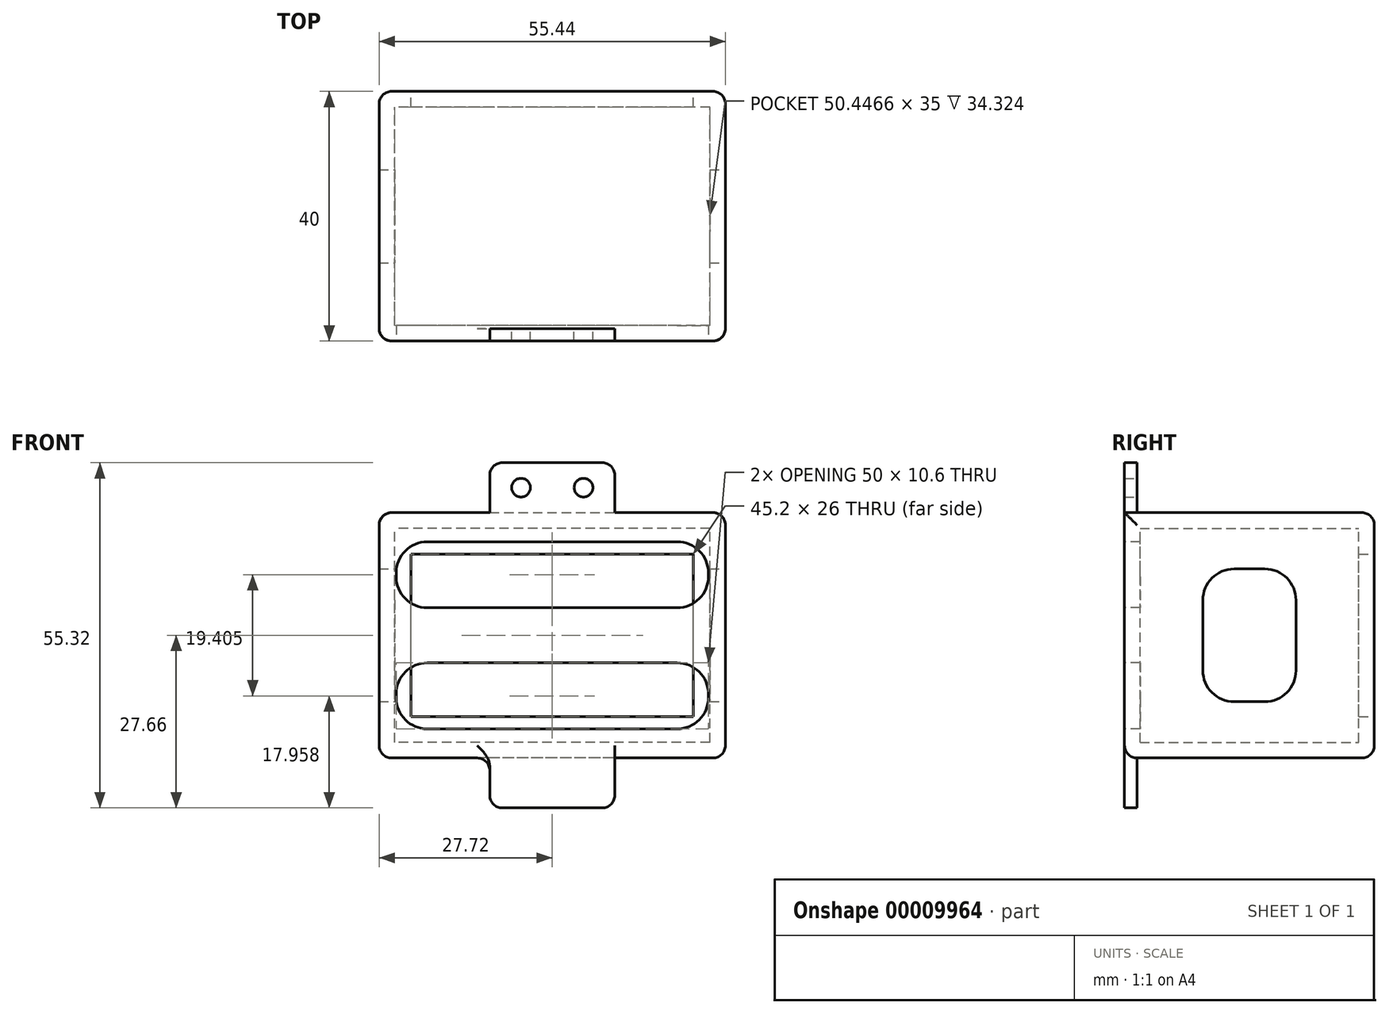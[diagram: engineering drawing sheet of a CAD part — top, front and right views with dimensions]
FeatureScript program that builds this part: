
annotation { "Feature Type Name" : "Feature", "Feature Type Description" : "" }
export const myFeature = defineFeature(function(context is Context, id is Id, definition is map)
    precondition{}
    {
        {
            var Q0;
            Q0=qCreatedBy(makeId("Front.planeOp"),FACE);
            var sketch = newSketch(context, id + "F0", { "sketchPlane" : qUnion([Q0])});
            skLineSegment(sketch, "E0.bottom", {"start": v(0, 0) * mm, "end": v(50, 0) * mm});
            skLineSegment(sketch, "E0.top", {"start": v(0, 30) * mm, "end": v(50, 30) * mm});
            skLineSegment(sketch, "E0.left", {"start": v(0, 0) * mm, "end": v(0, 30) * mm});
            skLineSegment(sketch, "E0.right", {"start": v(50, 0) * mm, "end": v(50, 30) * mm});
            skLineSegment(sketch, "E1", {"start": v(25, 30) * mm, "end": v(25, 0) * mm, "construction": true});
            skLineSegment(sketch, "E2", {"start": v(0, 15) * mm, "end": v(50, 15) * mm, "construction": true});
            skPoint(sketch, "E3", {"position": v(25, 15) * mm});
            skLineSegment(sketch, "E4.rect.bottom", {"start": v(47.6, 2) * mm, "end": v(2.4, 2) * mm});
            skLineSegment(sketch, "E4.rect.top", {"start": v(47.6, 28) * mm, "end": v(2.4, 28) * mm});
            skLineSegment(sketch, "E4.rect.left", {"start": v(47.6, 2) * mm, "end": v(47.6, 28) * mm});
            skLineSegment(sketch, "E4.rect.right", {"start": v(2.4, 2) * mm, "end": v(2.4, 28) * mm});
            skLineSegment(sketch, "E5.rect.bottom", {"start": v(52.72, -4.66) * mm, "end": v(-2.72, -4.66) * mm});
            skLineSegment(sketch, "E5.rect.top", {"start": v(52.72, 34.66) * mm, "end": v(-2.72, 34.66) * mm});
            skLineSegment(sketch, "E5.rect.left", {"start": v(52.72, -4.66) * mm, "end": v(52.72, 34.66) * mm});
            skLineSegment(sketch, "E5.rect.right", {"start": v(-2.72, -4.66) * mm, "end": v(-2.72, 34.66) * mm});
            skSolve(sketch);
        }
        {
            var Q0;
            Q0 = qSketchRegion(id + "F0", true);
            var Q1;
            Q1=makeQuery(id+"F0.imprint","IMPRINT",FACE,{"disambiguationData":[TD([[makeQuery(id+"F0.imprint","IMPRINT",EDGE,{"derivedFrom":sQuery(id+"F0.wireOp",EDGE,"E0.bottom")}),1.0]])]});
            var Q2;
            Q2=makeQuery(id+"F0.imprint","IMPRINT",FACE,{"disambiguationData":[TD([[makeQuery(id+"F0.imprint","IMPRINT",EDGE,{"derivedFrom":sQuery(id+"F0.wireOp",EDGE,"E4.rect.bottom")}),-1.0]])]});
            extrude(context, id + "F1", {"entities" : qUnion([Q0, Q1, Q2]), "depth" : 40 * mm});
        }
        {
            var Q0;
            Q0=makeQuery(id+"F1.opExtrude","CAP_FACE",FACE,{"disambiguationData":[OSD([sQuery(id+"F0.wireOp",EDGE,"E5.rect.bottom"),sQuery(id+"F0.wireOp",EDGE,"E5.rect.top"),sQuery(id+"F0.wireOp",EDGE,"E5.rect.left"),sQuery(id+"F0.wireOp",EDGE,"E5.rect.right")])],"isStart":false});
            var Q1;
            Q1=makeQuery(id+"F1.opExtrude","SWEPT_BODY",BODY,{"disambiguationData":[OSD([sQuery(id+"F0.wireOp",EDGE,"E5.rect.bottom"),sQuery(id+"F0.wireOp",EDGE,"E5.rect.top"),sQuery(id+"F0.wireOp",EDGE,"E5.rect.left"),sQuery(id+"F0.wireOp",EDGE,"E5.rect.right")])]});
            shell(context, id + "F2", {"isHollow" : true, "entities" : qUnion([Q0]), "parts" : qUnion([Q1]), "thickness" : 2.5 * mm});
        }
        {
            var Q0;
            Q0=makeQuery(id+"F0.imprint","IMPRINT",FACE,{"disambiguationData":[TD([[makeQuery(id+"F0.imprint","IMPRINT",EDGE,{"derivedFrom":sQuery(id+"F0.wireOp",EDGE,"E4.rect.bottom")}),-1.0]])]});
            extrude(context, id + "F3", {"entities" : qUnion([Q0]), "operationType" : NewBodyOperationType.REMOVE, "endBound" : BoundingType.UP_TO_NEXT, "depth" : 25 * mm});
        }
        {
            var Q0;
            Q0=makeQuery(id+"F1.opExtrude","CAP_FACE",FACE,{"disambiguationData":[OSD([sQuery(id+"F0.wireOp",EDGE,"E5.rect.bottom"),sQuery(id+"F0.wireOp",EDGE,"E5.rect.top"),sQuery(id+"F0.wireOp",EDGE,"E5.rect.left"),sQuery(id+"F0.wireOp",EDGE,"E5.rect.right")])],"isStart":false});
            var sketch = newSketch(context, id + "F4", { "sketchPlane" : qUnion([Q0])});
            skLineSegment(sketch, "E6.0", {"start": v(5, 30) * mm, "end": v(45, 30) * mm});
            skLineSegment(sketch, "E7.top", {"start": v(5, 19.4) * mm, "end": v(45, 19.4) * mm});
            skLineSegment(sketch, "E7.left", {"start": v(0, 25) * mm, "end": v(0, 24.4) * mm});
            skLineSegment(sketch, "E7.right", {"start": v(50, 25) * mm, "end": v(50, 24.4) * mm});
            skPoint(sketch, "E8.visualSharp", {"position": v(0, 30) * mm});
            skArc(sketch, "E8.filletArc", {"start": v(5, 30) * mm, "mid": v(1.46, 28.54) * mm, "end": v(0, 25) * mm});
            skPoint(sketch, "E9.visualSharp", {"position": v(50, 30) * mm});
            skArc(sketch, "E9.filletArc", {"start": v(50, 25) * mm, "mid": v(48.54, 28.54) * mm, "end": v(45, 30) * mm});
            skPoint(sketch, "E10.visualSharp", {"position": v(0, 19.4) * mm});
            skArc(sketch, "E10.filletArc", {"start": v(0, 24.4) * mm, "mid": v(1.46, 20.87) * mm, "end": v(5, 19.4) * mm});
            skPoint(sketch, "E11.visualSharp", {"position": v(50, 19.4) * mm});
            skArc(sketch, "E11.filletArc", {"start": v(45, 19.4) * mm, "mid": v(48.54, 20.87) * mm, "end": v(50, 24.4) * mm});
            skPoint(sketch, "E12.orphan", {"position": v(25, 0) * mm});
            skPoint(sketch, "E13.0.start.orphan", {"position": v(25, 30) * mm});
            skLineSegment(sketch, "E14.0", {"start": v(0, 15) * mm, "end": v(50, 15) * mm});
            skLineSegment(sketch, "E15.0.MirrorCS", {"start": v(5, 10.6) * mm, "end": v(45, 10.6) * mm});
            skArc(sketch, "E16.0.MirrorCS", {"start": v(45, 10.6) * mm, "mid": v(48.54, 9.13) * mm, "end": v(50, 5.6) * mm});
            skArc(sketch, "E17.0.MirrorCS", {"start": v(50, 5) * mm, "mid": v(48.54, 1.46) * mm, "end": v(45, 0) * mm});
            skLineSegment(sketch, "E18.0.MirrorCS", {"start": v(5, 0) * mm, "end": v(45, 0) * mm});
            skArc(sketch, "E19.0.MirrorCS", {"start": v(5, 0) * mm, "mid": v(1.46, 1.46) * mm, "end": v(0, 5) * mm});
            skArc(sketch, "E20.0.MirrorCS", {"start": v(0, 5.6) * mm, "mid": v(1.46, 9.13) * mm, "end": v(5, 10.6) * mm});
            skLineSegment(sketch, "E21.0.MirrorCS", {"start": v(0, 5) * mm, "end": v(0, 5.6) * mm});
            skLineSegment(sketch, "E22.0.MirrorCS", {"start": v(50, 5) * mm, "end": v(50, 5.6) * mm});
            skSolve(sketch);
        }
        {
            var Q0;
            Q0=makeQuery(id+"F4.imprint","IMPRINT",FACE,{"disambiguationData":[TD([[makeQuery(id+"F4.imprint","IMPRINT",EDGE,{"derivedFrom":sQuery(id+"F4.wireOp",EDGE,"E7.left")}),1.0]])]});
            var Q1;
            Q1=makeQuery(id+"F4.imprint","IMPRINT",FACE,{"disambiguationData":[TD([[makeQuery(id+"F4.imprint","IMPRINT",EDGE,{"derivedFrom":sQuery(id+"F4.wireOp",EDGE,"E7.right")}),-1.0]])]});
            var Q2;
            Q2=makeQuery(id+"F4.imprint","IMPRINT",FACE,{"disambiguationData":[TD([[makeQuery(id+"F4.imprint","IMPRINT",EDGE,{"derivedFrom":sQuery(id+"F4.wireOp",EDGE,"E15.0.MirrorCS")}),-1.0]])]});
            extrude(context, id + "F5", {"entities" : qUnion([Q0, Q1, Q2]), "operationType" : NewBodyOperationType.REMOVE, "endBound" : BoundingType.UP_TO_NEXT, "oppositeDirection" : true, "depth" : 25 * mm});
        }
        {
            var Q0;
            Q0=makeQuery(id+"F1.opExtrude","CAP_EDGE",EDGE,{"disambiguationData":[OSD([sQuery(id+"F0.wireOp",EDGE,"E5.rect.left")])],"isStart":true});
            var Q1;
            Q1=makeQuery(id+"F1.opExtrude","CAP_EDGE",EDGE,{"disambiguationData":[OSD([sQuery(id+"F0.wireOp",EDGE,"E5.rect.bottom")])],"isStart":true});
            var Q2;
            Q2=makeQuery(id+"F1.opExtrude","CAP_EDGE",EDGE,{"disambiguationData":[OSD([sQuery(id+"F0.wireOp",EDGE,"E5.rect.top")])],"isStart":true});
            var Q3;
            Q3=makeQuery(id+"F1.opExtrude","CAP_EDGE",EDGE,{"disambiguationData":[OSD([sQuery(id+"F0.wireOp",EDGE,"E5.rect.right")])],"isStart":true});
            fillet(context, id + "F6", {"entities" : qUnion([Q0, Q1, Q2, Q3]), "radius" : 2 * mm, "tangentPropagation" : true, "allowEdgeOverflow" : false});
        }
        {
            var Q0;
            Q0=makeQuery(id+"F1.opExtrude","SWEPT_FACE",FACE,{"disambiguationData":[OSD([sQuery(id+"F0.wireOp",EDGE,"E5.rect.bottom")])]});
            fillet(context, id + "F7", {"entities" : qUnion([Q0]), "radius" : 2 * mm, "tangentPropagation" : true, "allowEdgeOverflow" : false});
        }
        {
            var Q0;
            Q0=makeQuery(id+"F1.opExtrude","SWEPT_FACE",FACE,{"disambiguationData":[OSD([sQuery(id+"F0.wireOp",EDGE,"E5.rect.right")])]});
            fillet(context, id + "F8", {"entities" : qUnion([Q0]), "radius" : 2 * mm, "tangentPropagation" : true, "allowEdgeOverflow" : false});
        }
        {
            var Q0;
            Q0=makeQuery(id+"F1.opExtrude","SWEPT_FACE",FACE,{"disambiguationData":[OSD([sQuery(id+"F0.wireOp",EDGE,"E5.rect.left")])]});
            fillet(context, id + "F9", {"entities" : qUnion([Q0]), "radius" : 2 * mm, "tangentPropagation" : true, "allowEdgeOverflow" : false});
        }
        {
            var Q0;
            Q0=makeQuery(id+"F1.opExtrude","SWEPT_FACE",FACE,{"disambiguationData":[OSD([sQuery(id+"F0.wireOp",EDGE,"E5.rect.top")])]});
            var sketch = newSketch(context, id + "F10", { "sketchPlane" : qUnion([Q0])});
            skLineSegment(sketch, "E23", {"start": v(25, -38) * mm, "end": v(25, -2) * mm, "construction": true});
            skLineSegment(sketch, "E24.bottom", {"start": v(15, -38) * mm, "end": v(35, -38) * mm});
            skLineSegment(sketch, "E24.top", {"start": v(15, -40) * mm, "end": v(35, -40) * mm});
            skLineSegment(sketch, "E24.left", {"start": v(15, -38) * mm, "end": v(15, -40) * mm});
            skLineSegment(sketch, "E24.right", {"start": v(35, -38) * mm, "end": v(35, -40) * mm});
            skSolve(sketch);
        }
        {
            var Q0;
            Q0=makeQuery(id+"F10.imprint","IMPRINT",FACE,{"disambiguationData":[TD([[makeQuery(id+"F10.imprint","IMPRINT",EDGE,{"derivedFrom":sQuery(id+"F10.wireOp",EDGE,"E24.bottom")}),-1.0]])]});
            var Q1;
            Q1=makeQuery(id+"F5.boolean.opBoolean","COPY",FACE,{"derivedFrom":makeQuery(id+"F5.opExtrude","SWEPT_FACE",FACE,{"disambiguationData":[OSD([sQuery(id+"F4.wireOp",EDGE,"E6.0")])]})});
            extrude(context, id + "F11", {"entities" : qUnion([Q0]), "operationType" : NewBodyOperationType.ADD, "depth" : 8 * mm, "hasSecondDirection" : true, "secondDirectionBound" : SecondDirectionBoundingType.UP_TO_SURFACE, "secondDirectionOppositeDirection" : true, "secondDirectionBoundEntityFace" : qUnion([Q1]), "secondDirectionDepth" : 25 * mm});
        }
        {
            var Q0;
            {var subQ0=sQuery(id+"F0.wireOp",EDGE,"E5.rect.top");Q0=makeQuery(id+"F11.boolean.opBoolean","INTERSECT",EDGE,{"derivedFrom":[makeQuery(id+"F6.opFillet","BLEND_FACE",FACE,{"disambiguationData":[OSD([subQ0]),TDD([makeQuery(id+"F1.opExtrude","CAP_EDGE",EDGE,{"disambiguationData":[OSD([subQ0])],"isStart":false})])]}),makeQuery(id+"F11.opExtrude","SWEPT_FACE",FACE,{"disambiguationData":[OSD([sQuery(id+"F10.wireOp",EDGE,"E24.right")])]})]});}
            var Q1;
            Q1=makeQuery(id+"F11.opExtrude","CAP_EDGE",EDGE,{"disambiguationData":[OSD([sQuery(id+"F10.wireOp",EDGE,"E24.right")])],"isStart":false});
            var Q2;
            Q2=makeQuery(id+"F11.opExtrude","CAP_EDGE",EDGE,{"disambiguationData":[OSD([sQuery(id+"F10.wireOp",EDGE,"E24.left")])],"isStart":false});
            var Q3;
            {var subQ0=sQuery(id+"F0.wireOp",EDGE,"E5.rect.top");Q3=makeQuery(id+"F11.boolean.opBoolean","INTERSECT",EDGE,{"derivedFrom":[makeQuery(id+"F6.opFillet","BLEND_FACE",FACE,{"disambiguationData":[OSD([subQ0]),TDD([makeQuery(id+"F1.opExtrude","CAP_EDGE",EDGE,{"disambiguationData":[OSD([subQ0])],"isStart":false})])]}),makeQuery(id+"F11.opExtrude","SWEPT_FACE",FACE,{"disambiguationData":[OSD([sQuery(id+"F10.wireOp",EDGE,"E24.left")])]})]});}
            fillet(context, id + "F12", {"entities" : qUnion([Q0, Q1, Q2, Q3]), "radius" : 2 * mm, "tangentPropagation" : true, "allowEdgeOverflow" : false});
        }
        {
            var Q0;
            Q0=makeQuery(id+"F11.opExtrude","SWEPT_FACE",FACE,{"disambiguationData":[OSD([sQuery(id+"F10.wireOp",EDGE,"E24.bottom")])]});
            var sketch = newSketch(context, id + "F13", { "sketchPlane" : qUnion([Q0])});
            skLineSegment(sketch, "E25", {"start": v(-25, 42.66) * mm, "end": v(-25, 34.66) * mm, "construction": true});
            skLineSegment(sketch, "E26", {"start": v(-35, 38.66) * mm, "end": v(-31.5, 38.66) * mm, "construction": true});
            skCircle(sketch, "E27", {"center": v(-30, 38.66) * mm, "radius": 1.5 * mm});
            skCircle(sketch, "E28", {"center": v(-20, 38.66) * mm, "radius": 1.5 * mm});
            skLineSegment(sketch, "E29", {"start": v(-25, 38.66) * mm, "end": v(-21.5, 38.66) * mm, "construction": true});
            skLineSegment(sketch, "E30.trimOffspring", {"start": v(-28.5, 38.66) * mm, "end": v(-25, 38.66) * mm, "construction": true});
            skLineSegment(sketch, "E31.trimOffspring", {"start": v(-18.5, 38.66) * mm, "end": v(-15, 38.66) * mm, "construction": true});
            skLineSegment(sketch, "E32.0", {"start": v(0, 15) * mm, "end": v(-50, 15) * mm});
            skCircle(sketch, "E33.0.MirrorC", {"center": v(-30, -8.66) * mm, "radius": 1.5 * mm});
            skCircle(sketch, "E34.0.MirrorC", {"center": v(-20, -8.66) * mm, "radius": 1.5 * mm});
            skSolve(sketch);
        }
        {
            var Q0;
            Q0=makeQuery(id+"F1.opExtrude","SWEPT_FACE",FACE,{"disambiguationData":[OSD([sQuery(id+"F0.wireOp",EDGE,"E5.rect.bottom")])]});
            var sketch = newSketch(context, id + "F14", { "sketchPlane" : qUnion([Q0])});
            skLineSegment(sketch, "E35.0", {"start": v(35, 38) * mm, "end": v(35, 40) * mm});
            skLineSegment(sketch, "E36.0", {"start": v(15, 38) * mm, "end": v(15, 40) * mm});
            skLineSegment(sketch, "E37.0", {"start": v(35, 38) * mm, "end": v(15, 38) * mm});
            skPoint(sketch, "E38.orphan", {"position": v(-0.72, 38) * mm});
            skPoint(sketch, "E39.orphan", {"position": v(50.72, 38) * mm});
            skLineSegment(sketch, "E40.0", {"start": v(15, 40) * mm, "end": v(35, 40) * mm});
            skPoint(sketch, "E41.orphan", {"position": v(5, 40) * mm});
            skPoint(sketch, "E42.orphan", {"position": v(45, 40) * mm});
            skSolve(sketch);
        }
        {
            var Q0;
            Q0=makeQuery(id+"F14.imprint","IMPRINT",FACE,{"disambiguationData":[TD([[makeQuery(id+"F14.imprint","IMPRINT",EDGE,{"derivedFrom":sQuery(id+"F14.wireOp",EDGE,"E35.0")}),1.0]])]});
            extrude(context, id + "F15", {"entities" : qUnion([Q0]), "operationType" : NewBodyOperationType.ADD, "depth" : 8 * mm, "hasSecondDirection" : true, "secondDirectionBound" : SecondDirectionBoundingType.UP_TO_NEXT, "secondDirectionOppositeDirection" : true, "secondDirectionDepth" : 25 * mm});
        }
        {
            var Q0;
            Q0=makeQuery(id+"F13.imprint","IMPRINT",FACE,{"disambiguationData":[TD([[makeQuery(id+"F13.imprint","IMPRINT",EDGE,{"derivedFrom":sQuery(id+"F13.wireOp",EDGE,"E27")}),1.0]])]});
            var Q1;
            Q1=makeQuery(id+"F13.imprint","IMPRINT",FACE,{"disambiguationData":[TD([[makeQuery(id+"F13.imprint","IMPRINT",EDGE,{"derivedFrom":sQuery(id+"F13.wireOp",EDGE,"E28")}),1.0]])]});
            var Q2;
            Q2=makeQuery(id+"F13.imprint","IMPRINT",FACE,{"disambiguationData":[TD([[makeQuery(id+"F13.imprint","IMPRINT",EDGE,{"derivedFrom":sQuery(id+"F13.wireOp",EDGE,"E34.0.MirrorC")}),-1.0]])]});
            var Q3;
            Q3=makeQuery(id+"F13.imprint","IMPRINT",FACE,{"disambiguationData":[TD([[makeQuery(id+"F13.imprint","IMPRINT",EDGE,{"derivedFrom":sQuery(id+"F13.wireOp",EDGE,"E33.0.MirrorC")}),-1.0]])]});
            var Q4;
            Q4=sQuery(id+"F13.wireOp",EDGE,"E27");
            var Q5;
            Q5=sQuery(id+"F13.wireOp",EDGE,"E28");
            extrude(context, id + "F16", {"entities" : qUnion([Q0, Q1, Q2, Q3]), "operationType" : NewBodyOperationType.REMOVE, "surfaceEntities" : qUnion([Q4, Q5]), "endBound" : BoundingType.THROUGH_ALL, "oppositeDirection" : true, "depth" : 25 * mm});
        }
        {
            var Q0;
            Q0=makeQuery(id+"F15.opExtrude","CAP_EDGE",EDGE,{"disambiguationData":[OSD([sQuery(id+"F14.wireOp",EDGE,"E36.0")])],"isStart":false});
            var Q1;
            Q1=makeQuery(id+"F15.opExtrude","TWEAK_EDGE",EDGE,{"derivedFrom":[makeQuery(id+"F7.opFillet","BLEND_FACE",FACE,{"disambiguationData":[OSD([sQuery(id+"F0.wireOp",EDGE,"E5.rect.bottom")])]}),makeQuery(id+"F14.imprint","IMPRINT",EDGE,{"derivedFrom":sQuery(id+"F14.wireOp",EDGE,"E36.0")})]});
            var Q2;
            Q2=makeQuery(id+"F15.opExtrude","CAP_EDGE",EDGE,{"disambiguationData":[OSD([sQuery(id+"F14.wireOp",EDGE,"E35.0")])],"isStart":false});
            var Q3;
            Q3=makeQuery(id+"F15.opExtrude","TWEAK_EDGE",EDGE,{"derivedFrom":[makeQuery(id+"F7.opFillet","BLEND_FACE",FACE,{"disambiguationData":[OSD([sQuery(id+"F0.wireOp",EDGE,"E5.rect.bottom")])]}),makeQuery(id+"F14.imprint","IMPRINT",EDGE,{"derivedFrom":sQuery(id+"F14.wireOp",EDGE,"E35.0")})]});
            fillet(context, id + "F17", {"entities" : qUnion([Q0, Q1, Q2, Q3]), "radius" : 2 * mm, "tangentPropagation" : true, "allowEdgeOverflow" : false});
        }
        {
            var Q0;
            Q0=makeQuery(id+"F1.opExtrude","SWEPT_FACE",FACE,{"disambiguationData":[OSD([sQuery(id+"F0.wireOp",EDGE,"E5.rect.left")])]});
            var sketch = newSketch(context, id + "F18", { "sketchPlane" : qUnion([Q0])});
            skLineSegment(sketch, "E43.rect.bottom", {"start": v(-22.46, 4.37) * mm, "end": v(-17.54, 4.37) * mm});
            skLineSegment(sketch, "E43.rect.top", {"start": v(-22.46, 25.63) * mm, "end": v(-17.54, 25.63) * mm});
            skLineSegment(sketch, "E43.rect.left", {"start": v(-27.46, 9.37) * mm, "end": v(-27.46, 20.63) * mm});
            skLineSegment(sketch, "E43.rect.right", {"start": v(-12.54, 9.37) * mm, "end": v(-12.54, 20.63) * mm});
            skPoint(sketch, "E43.rect.middle", {"position": v(-20, 15) * mm});
            skLineSegment(sketch, "E44", {"start": v(-20, 32.66) * mm, "end": v(-20, -2.66) * mm, "construction": true});
            skPoint(sketch, "E45.visualSharp", {"position": v(-12.54, 25.63) * mm});
            skArc(sketch, "E45.filletArc", {"start": v(-12.54, 20.63) * mm, "mid": v(-14, 24.17) * mm, "end": v(-17.54, 25.63) * mm});
            skPoint(sketch, "E46.visualSharp", {"position": v(-27.46, 4.37) * mm});
            skArc(sketch, "E46.filletArc", {"start": v(-27.46, 9.37) * mm, "mid": v(-26, 5.83) * mm, "end": v(-22.46, 4.37) * mm});
            skPoint(sketch, "E47.visualSharp", {"position": v(-12.54, 4.37) * mm});
            skArc(sketch, "E47.filletArc", {"start": v(-17.54, 4.37) * mm, "mid": v(-14, 5.83) * mm, "end": v(-12.54, 9.37) * mm});
            skPoint(sketch, "E48.visualSharp", {"position": v(-27.46, 25.63) * mm});
            skArc(sketch, "E48.filletArc", {"start": v(-22.46, 25.63) * mm, "mid": v(-26, 24.17) * mm, "end": v(-27.46, 20.63) * mm});
            skSolve(sketch);
        }
        {
            var Q0;
            Q0=makeQuery(id+"F18.imprint","IMPRINT",FACE,{"disambiguationData":[TD([[makeQuery(id+"F18.imprint","IMPRINT",EDGE,{"derivedFrom":sQuery(id+"F18.wireOp",EDGE,"E43.rect.bottom")}),1.0]])]});
            extrude(context, id + "F19", {"entities" : qUnion([Q0]), "operationType" : NewBodyOperationType.REMOVE, "endBound" : BoundingType.THROUGH_ALL, "oppositeDirection" : true, "depth" : 25 * mm});
        }
    });
